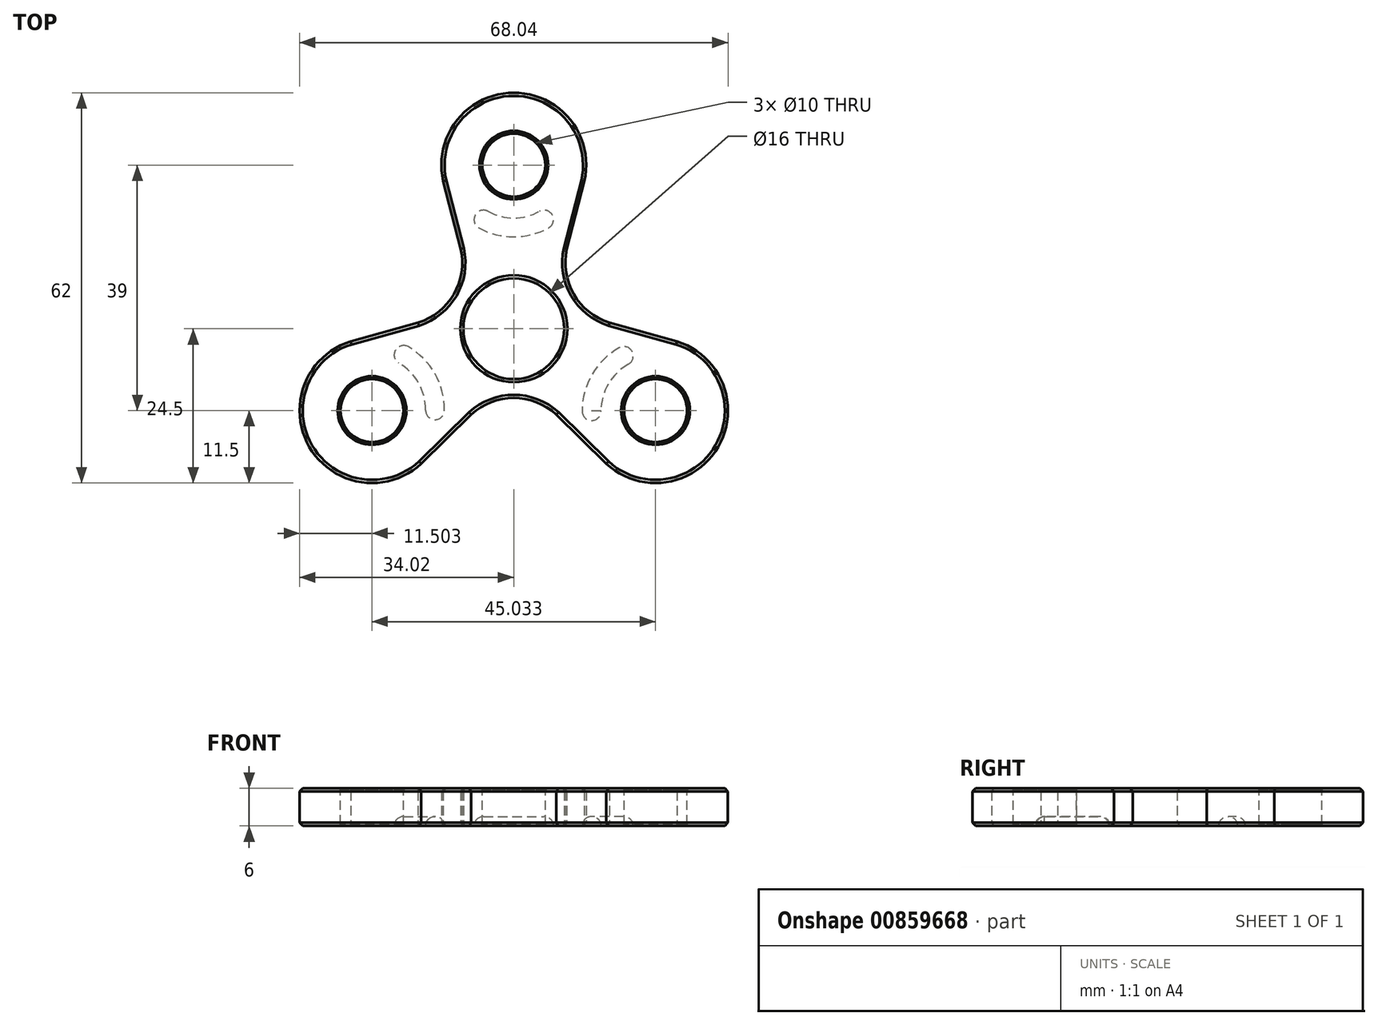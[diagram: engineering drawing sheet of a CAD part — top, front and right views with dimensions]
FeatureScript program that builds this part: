
annotation { "Feature Type Name" : "Feature", "Feature Type Description" : "" }
export const myFeature = defineFeature(function(context is Context, id is Id, definition is map)
    precondition{}
    {
        {
            var Q0;
            Q0=qCreatedBy(makeId("Top.planeOp"),FACE);
            var sketch = newSketch(context, id + "F0", { "sketchPlane" : qUnion([Q0])});
            skCircle(sketch, "E0", {"center": v(0, 0) * mm, "radius": 37.5 * mm, "construction": true});
            skCircle(sketch, "E1", {"center": v(0, 0) * mm, "radius": 26 * mm, "construction": true});
            skCircle(sketch, "E2", {"center": v(0, 0) * mm, "radius": 21 * mm, "construction": true});
            skLineSegment(sketch, "E3", {"start": v(0, 0) * mm, "end": v(0, 58.55) * mm, "construction": true});
            skLineSegment(sketch, "E4", {"start": v(0, 0) * mm, "end": v(51.06, -29.48) * mm, "construction": true});
            skLineSegment(sketch, "E5", {"start": v(0, 0) * mm, "end": v(-53.04, -30.62) * mm, "construction": true});
            skArc(sketch, "E6", {"start": v(11.22, 23.46) * mm, "mid": v(0, 37.5) * mm, "end": v(-11.22, 23.46) * mm});
            skArc(sketch, "E7", {"start": v(14.7, -21.44) * mm, "mid": v(32.48, -18.75) * mm, "end": v(25.92, -2.02) * mm});
            skArc(sketch, "E8", {"start": v(-25.92, -2.02) * mm, "mid": v(-32.48, -18.75) * mm, "end": v(-14.7, -21.44) * mm});
            skLineSegment(sketch, "E9", {"start": v(0, 0) * mm, "end": v(65.3, 37.7) * mm, "construction": true});
            skLineSegment(sketch, "E10", {"start": v(0, 0) * mm, "end": v(-64.4, 37.18) * mm, "construction": true});
            skLineSegment(sketch, "E11", {"start": v(0, 0) * mm, "end": v(0, -53.5) * mm, "construction": true});
            skArc(sketch, "E12", {"start": v(8.43, 12.68) * mm, "mid": v(9.53, 5.5) * mm, "end": v(15.2, 0.96) * mm});
            skArc(sketch, "E13", {"start": v(6.77, -13.64) * mm, "mid": v(0, -11) * mm, "end": v(-6.77, -13.64) * mm});
            skArc(sketch, "E14", {"start": v(-15.2, 0.96) * mm, "mid": v(-9.53, 5.5) * mm, "end": v(-8.43, 12.68) * mm});
            skLineSegment(sketch, "E15", {"start": v(8.43, 12.68) * mm, "end": v(11.22, 23.46) * mm});
            skLineSegment(sketch, "E16", {"start": v(-8.43, 12.68) * mm, "end": v(-11.22, 23.46) * mm});
            skLineSegment(sketch, "E17", {"start": v(15.2, 0.96) * mm, "end": v(25.92, -2.02) * mm});
            skLineSegment(sketch, "E18", {"start": v(6.77, -13.64) * mm, "end": v(14.7, -21.44) * mm});
            skLineSegment(sketch, "E19", {"start": v(-6.77, -13.64) * mm, "end": v(-14.7, -21.44) * mm});
            skLineSegment(sketch, "E20", {"start": v(-15.2, 0.96) * mm, "end": v(-25.92, -2.02) * mm});
            skCircle(sketch, "E21", {"center": v(0, 0) * mm, "radius": 8 * mm});
            skLineSegment(sketch, "E22", {"start": v(-22.52, -13) * mm, "end": v(-25.92, -2.02) * mm, "construction": true});
            skLineSegment(sketch, "E23", {"start": v(-15.2, 0.96) * mm, "end": v(-41.39, -14.16) * mm, "construction": true});
            skLineSegment(sketch, "E24", {"start": v(-22.52, -13) * mm, "end": v(-14.7, -21.44) * mm, "construction": true});
            skSolve(sketch);
        }
        {
            var Q0;
            Q0 = qSketchRegion(id + "F0", true);
            extrude(context, id + "F1", {"entities" : qUnion([Q0]), "depth" : 6 * mm, "offsetDistance" : 25 * mm});
        }
        {
            var Q0;
            Q0=makeQuery(id+"F1.opExtrude","CAP_FACE",FACE,{"disambiguationData":[OSD([sQuery(id+"F0.wireOp",EDGE,"E6"),sQuery(id+"F0.wireOp",EDGE,"E7"),sQuery(id+"F0.wireOp",EDGE,"E8"),sQuery(id+"F0.wireOp",EDGE,"E12"),sQuery(id+"F0.wireOp",EDGE,"E13"),sQuery(id+"F0.wireOp",EDGE,"E14"),sQuery(id+"F0.wireOp",EDGE,"bWhlO0tW-kghy-6alH-HDye-0pY6NdsW0tyK"),sQuery(id+"F0.wireOp",EDGE,"dD2nLPx4-apQZ-kcct-oE38-IG9Xx2rJx7vh"),sQuery(id+"F0.wireOp",EDGE,"bGNLzmFQ-ohA0-4ANv-BgA9-OSxseYt1keDi"),sQuery(id+"F0.wireOp",EDGE,"IjS9LlBg-qYSG-hjFQ-nDQx-gUHvTnkpquyT"),sQuery(id+"F0.wireOp",EDGE,"3twbZAZV-WnEQ-h6Eq-sG5d-3KfLWMJG8j8c"),sQuery(id+"F0.wireOp",EDGE,"Pv3vPwHN-Bdnd-p7Uw-Mw2V-DmqJswefJnMi"),sQuery(id+"F0.wireOp",EDGE,"DhiOcpT5-T1U3-qdIw-KOjH-1pIkxhC2DhTk")])],"isStart":false});
            var sketch = newSketch(context, id + "F2", { "sketchPlane" : qUnion([Q0])});
            skCircle(sketch, "E25", {"center": v(22.52, -13) * mm, "radius": 5 * mm});
            skCircle(sketch, "E26", {"center": v(-22.52, -13) * mm, "radius": 5 * mm});
            skCircle(sketch, "E27", {"center": v(0, 26) * mm, "radius": 5 * mm});
            skSolve(sketch);
        }
        {
            var Q0;
            Q0 = qSketchRegion(id + "F2", true);
            extrude(context, id + "F3", {"entities" : qUnion([Q0]), "operationType" : NewBodyOperationType.REMOVE, "oppositeDirection" : true, "depth" : 25 * mm, "offsetDistance" : 25 * mm});
        }
        {
            var Q0;
            Q0=makeQuery(id+"F3.boolean.opBoolean","COPY",FACE,{"derivedFrom":makeQuery(id+"F3.opExtrude","SWEPT_FACE",FACE,{"disambiguationData":[OSD([sQuery(id+"F2.wireOp",EDGE,"E27")])]})});
            var Q1;
            Q1=makeQuery(id+"F1.opExtrude","SWEPT_FACE",FACE,{"disambiguationData":[OSD([sQuery(id+"F0.wireOp",EDGE,"DhiOcpT5-T1U3-qdIw-KOjH-1pIkxhC2DhTk")])]});
            var Q2;
            Q2=makeQuery(id+"F3.boolean.opBoolean","COPY",FACE,{"derivedFrom":makeQuery(id+"F3.opExtrude","SWEPT_FACE",FACE,{"disambiguationData":[OSD([sQuery(id+"F2.wireOp",EDGE,"E25")])]})});
            var Q3;
            Q3=makeQuery(id+"F3.boolean.opBoolean","COPY",FACE,{"derivedFrom":makeQuery(id+"F3.opExtrude","SWEPT_FACE",FACE,{"disambiguationData":[OSD([sQuery(id+"F2.wireOp",EDGE,"E26")])]})});
            chamfer(context, id + "F4", {"entities" : qUnion([Q0, Q1, Q2, Q3]), "width" : 0.25 * mm, "tangentPropagation" : true});
        }
        {
            var Q0;
            Q0=makeQuery(id+"F1.opExtrude","CAP_FACE",FACE,{"disambiguationData":[OSD([sQuery(id+"F0.wireOp",EDGE,"E6"),sQuery(id+"F0.wireOp",EDGE,"E7"),sQuery(id+"F0.wireOp",EDGE,"E8"),sQuery(id+"F0.wireOp",EDGE,"E12"),sQuery(id+"F0.wireOp",EDGE,"E13"),sQuery(id+"F0.wireOp",EDGE,"E14"),sQuery(id+"F0.wireOp",EDGE,"E15"),sQuery(id+"F0.wireOp",EDGE,"E16"),sQuery(id+"F0.wireOp",EDGE,"E17"),sQuery(id+"F0.wireOp",EDGE,"E18"),sQuery(id+"F0.wireOp",EDGE,"E19"),sQuery(id+"F0.wireOp",EDGE,"E20"),sQuery(id+"F0.wireOp",EDGE,"E21")])],"isStart":false});
            var Q1;
            Q1=makeQuery(id+"F1.opExtrude","CAP_FACE",FACE,{"disambiguationData":[OSD([sQuery(id+"F0.wireOp",EDGE,"E6"),sQuery(id+"F0.wireOp",EDGE,"E7"),sQuery(id+"F0.wireOp",EDGE,"E8"),sQuery(id+"F0.wireOp",EDGE,"E12"),sQuery(id+"F0.wireOp",EDGE,"E13"),sQuery(id+"F0.wireOp",EDGE,"E14"),sQuery(id+"F0.wireOp",EDGE,"E15"),sQuery(id+"F0.wireOp",EDGE,"E16"),sQuery(id+"F0.wireOp",EDGE,"E17"),sQuery(id+"F0.wireOp",EDGE,"E18"),sQuery(id+"F0.wireOp",EDGE,"E19"),sQuery(id+"F0.wireOp",EDGE,"E20"),sQuery(id+"F0.wireOp",EDGE,"E21")])],"isStart":true});
            chamfer(context, id + "F5", {"entities" : qUnion([Q0, Q1]), "width" : 0.5 * mm, "tangentPropagation" : true});
        }
        {
            var Q0;
            Q0=makeQuery(id+"F0.imprint","IMPRINT",FACE,{"disambiguationData":[TD([[makeQuery(id+"F0.imprint","IMPRINT",EDGE,{"derivedFrom":sQuery(id+"F0.wireOp",EDGE,"E6")}),1.0]])]});
            var sketch = newSketch(context, id + "F6", { "sketchPlane" : qUnion([Q0])});
            skArc(sketch, "E28", {"start": v(-4.8, 17.35) * mm, "mid": v(0, 16.11) * mm, "end": v(4.8, 17.35) * mm});
            skArc(sketch, "E29", {"start": v(-12.51, -12.94) * mm, "mid": v(-13.82, -7.87) * mm, "end": v(-17.51, -4.16) * mm});
            skArc(sketch, "E30", {"start": v(17.47, -4.33) * mm, "mid": v(13.72, -8.01) * mm, "end": v(12.36, -13.09) * mm});
            skArc(sketch, "E31.0.startCap", {"start": v(-5.53, 16.03) * mm, "mid": v(-6.12, 18.07) * mm, "end": v(-4.09, 18.66) * mm});
            skArc(sketch, "E31.0.endCap", {"start": v(4.09, 18.66) * mm, "mid": v(6.12, 18.07) * mm, "end": v(5.53, 16.03) * mm});
            skArc(sketch, "E31.0.left", {"start": v(-4.09, 18.66) * mm, "mid": v(0, 17.61) * mm, "end": v(4.09, 18.66) * mm});
            skArc(sketch, "E31.0.right", {"start": v(-5.53, 16.03) * mm, "mid": v(0, 14.61) * mm, "end": v(5.53, 16.03) * mm});
            skArc(sketch, "E31.1.startCap", {"start": v(-11.01, -12.96) * mm, "mid": v(-12.53, -14.44) * mm, "end": v(-14.01, -12.92) * mm});
            skArc(sketch, "E31.1.endCap", {"start": v(-18.26, -5.46) * mm, "mid": v(-18.81, -3.41) * mm, "end": v(-16.76, -2.86) * mm});
            skArc(sketch, "E31.1.left", {"start": v(-14.01, -12.92) * mm, "mid": v(-15.13, -8.62) * mm, "end": v(-18.26, -5.46) * mm});
            skArc(sketch, "E31.1.right", {"start": v(-11.01, -12.96) * mm, "mid": v(-12.52, -7.13) * mm, "end": v(-16.76, -2.86) * mm});
            skArc(sketch, "E31.2.startCap", {"start": v(16.74, -3.02) * mm, "mid": v(18.78, -3.6) * mm, "end": v(18.2, -5.64) * mm});
            skArc(sketch, "E31.2.endCap", {"start": v(13.86, -13.08) * mm, "mid": v(12.36, -14.59) * mm, "end": v(10.86, -13.1) * mm});
            skArc(sketch, "E31.2.left", {"start": v(18.2, -5.64) * mm, "mid": v(15.02, -8.77) * mm, "end": v(13.86, -13.08) * mm});
            skArc(sketch, "E31.2.right", {"start": v(16.74, -3.02) * mm, "mid": v(12.43, -7.25) * mm, "end": v(10.86, -13.1) * mm});
            skSolve(sketch);
        }
        {
            var Q0;
            Q0 = qSketchRegion(id + "F6", true);
            extrude(context, id + "F7", {"entities" : qUnion([Q0]), "operationType" : NewBodyOperationType.REMOVE, "depth" : 1.5 * mm, "offsetDistance" : 25 * mm});
        }
        {
            var Q0;
            Q0=makeQuery(id+"F7.boolean.opBoolean","COPY",EDGE,{"derivedFrom":makeQuery(id+"F7.opExtrude","CAP_EDGE",EDGE,{"disambiguationData":[OSD([sQuery(id+"F6.wireOp",EDGE,"E31.0.left")])],"isStart":false})});
            var Q1;
            Q1=makeQuery(id+"F7.boolean.opBoolean","COPY",EDGE,{"derivedFrom":makeQuery(id+"F7.opExtrude","CAP_EDGE",EDGE,{"disambiguationData":[OSD([sQuery(id+"F6.wireOp",EDGE,"E31.1.right")])],"isStart":false})});
            var Q2;
            Q2=makeQuery(id+"F7.boolean.opBoolean","COPY",EDGE,{"derivedFrom":makeQuery(id+"F7.opExtrude","CAP_EDGE",EDGE,{"disambiguationData":[OSD([sQuery(id+"F6.wireOp",EDGE,"E31.2.right")])],"isStart":false})});
            fillet(context, id + "F8", {"entities" : qUnion([Q0, Q1, Q2]), "radius" : 1.5 * mm, "tangentPropagation" : true, "allowEdgeOverflow" : false});
        }
    });
